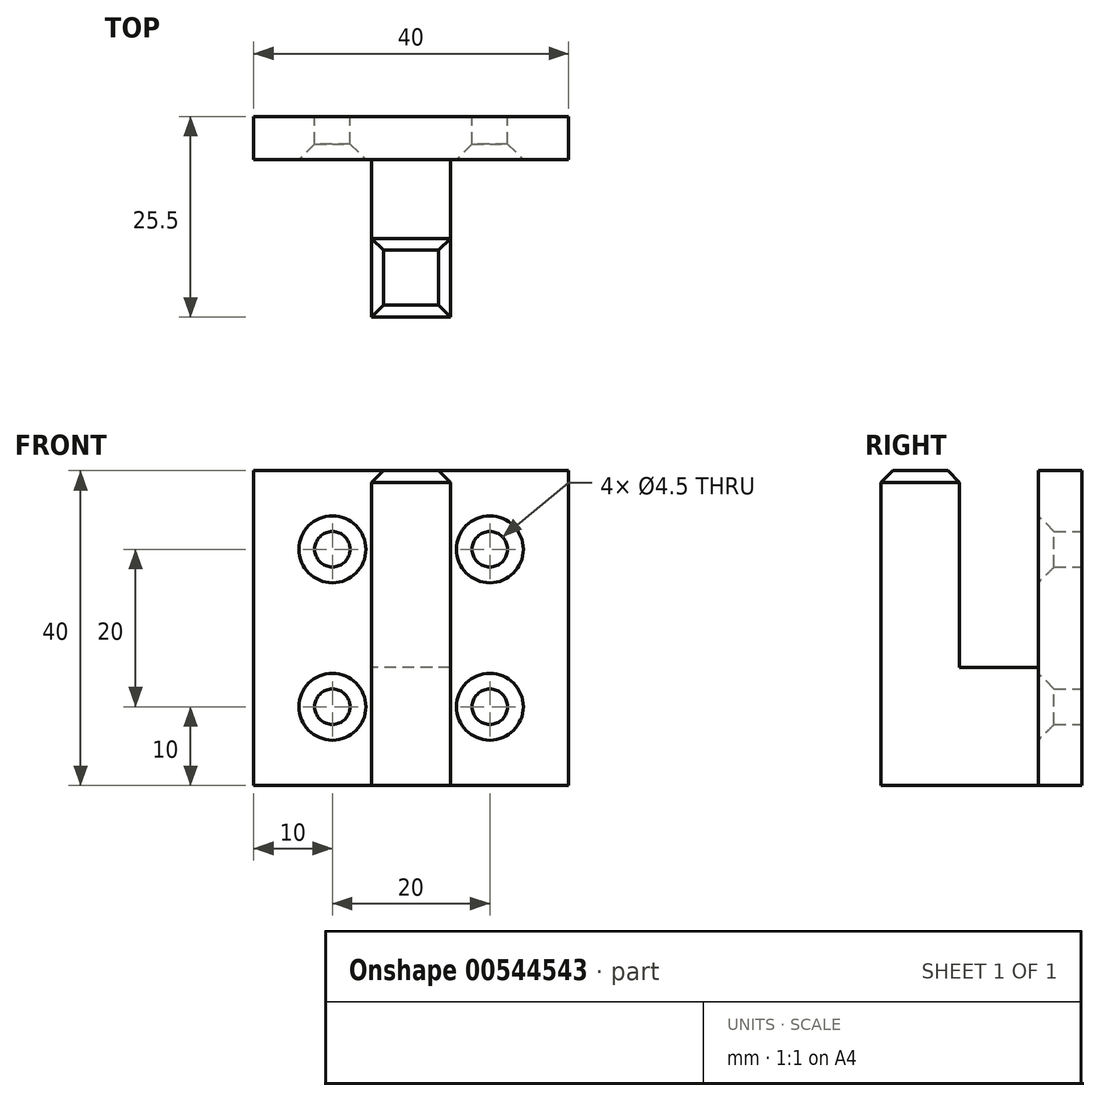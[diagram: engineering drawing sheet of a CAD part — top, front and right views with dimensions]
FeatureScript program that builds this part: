
annotation { "Feature Type Name" : "Feature", "Feature Type Description" : "" }
export const myFeature = defineFeature(function(context is Context, id is Id, definition is map)
    precondition{}
    {
        {
            var Q0;
            Q0=qCreatedBy(makeId("Front.planeOp"),FACE);
            var sketch = newSketch(context, id + "F0", { "sketchPlane" : qUnion([Q0])});
            skLineSegment(sketch, "E0", {"start": v(0, 0) * mm, "end": v(40, 0) * mm});
            skLineSegment(sketch, "E1", {"start": v(40, 0) * mm, "end": v(40, 40) * mm});
            skLineSegment(sketch, "E2", {"start": v(40, 40) * mm, "end": v(0, 40) * mm});
            skLineSegment(sketch, "E3", {"start": v(0, 40) * mm, "end": v(0, 0) * mm});
            skLineSegment(sketch, "E4", {"start": v(0, 40) * mm, "end": v(40, 0) * mm, "construction": true});
            skLineSegment(sketch, "E5", {"start": v(40, 40) * mm, "end": v(0, 0) * mm, "construction": true});
            skPoint(sketch, "E6", {"position": v(20, 20) * mm});
            skLineSegment(sketch, "E7", {"start": v(40, 40) * mm, "end": v(30, 30) * mm, "construction": true});
            skPoint(sketch, "E8", {"position": v(30, 30) * mm});
            skPoint(sketch, "E9.1.0", {"position": v(10, 30) * mm});
            skPoint(sketch, "E9.2.0", {"position": v(10, 10) * mm});
            skPoint(sketch, "E9.3.0", {"position": v(30, 10) * mm});
            skCircle(sketch, "E10", {"center": v(10, 30) * mm, "radius": 2.25 * mm});
            skCircle(sketch, "E11", {"center": v(30, 30) * mm, "radius": 2.25 * mm});
            skCircle(sketch, "E12", {"center": v(30, 10) * mm, "radius": 2.25 * mm});
            skCircle(sketch, "E13", {"center": v(10, 10) * mm, "radius": 2.25 * mm});
            skSolve(sketch);
        }
        {
            var Q0;
            Q0=makeQuery(id+"F0.imprint","IMPRINT",FACE,{"disambiguationData":[TD([[makeQuery(id+"F0.imprint","IMPRINT",EDGE,{"derivedFrom":sQuery(id+"F0.wireOp",EDGE,"E0")}),1.0]])]});
            extrude(context, id + "F1", {"entities" : qUnion([Q0]), "depth" : 5.5 * mm, "offsetDistance" : 25 * mm});
        }
        {
            var Q0;
            Q0=makeQuery(id+"F1.opExtrude","CAP_EDGE",EDGE,{"disambiguationData":[OSD([sQuery(id+"F0.wireOp",EDGE,"E10")])],"isStart":false});
            var Q1;
            Q1=makeQuery(id+"F1.opExtrude","CAP_EDGE",EDGE,{"disambiguationData":[OSD([sQuery(id+"F0.wireOp",EDGE,"E11")])],"isStart":false});
            var Q2;
            Q2=makeQuery(id+"F1.opExtrude","CAP_EDGE",EDGE,{"disambiguationData":[OSD([sQuery(id+"F0.wireOp",EDGE,"E12")])],"isStart":false});
            var Q3;
            Q3=makeQuery(id+"F1.opExtrude","CAP_EDGE",EDGE,{"disambiguationData":[OSD([sQuery(id+"F0.wireOp",EDGE,"E13")])],"isStart":false});
            chamfer(context, id + "F2", {"entities" : qUnion([Q0, Q1, Q2, Q3]), "width" : 2 * mm, "tangentPropagation" : true});
        }
        {
            var Q0;
            Q0=makeQuery(id+"F1.opExtrude","CAP_FACE",FACE,{"disambiguationData":[OSD([sQuery(id+"F0.wireOp",EDGE,"E0"),sQuery(id+"F0.wireOp",EDGE,"E1"),sQuery(id+"F0.wireOp",EDGE,"E2"),sQuery(id+"F0.wireOp",EDGE,"E3"),sQuery(id+"F0.wireOp",EDGE,"E10"),sQuery(id+"F0.wireOp",EDGE,"E11"),sQuery(id+"F0.wireOp",EDGE,"E12"),sQuery(id+"F0.wireOp",EDGE,"E13")])],"isStart":false});
            var sketch = newSketch(context, id + "F3", { "sketchPlane" : qUnion([Q0])});
            skLineSegment(sketch, "E14", {"start": v(0, 0) * mm, "end": v(15, 0) * mm, "construction": true});
            skLineSegment(sketch, "E15", {"start": v(15, 0) * mm, "end": v(25, 0) * mm});
            skLineSegment(sketch, "E16", {"start": v(25, 0) * mm, "end": v(25, 15) * mm});
            skLineSegment(sketch, "E17", {"start": v(25, 15) * mm, "end": v(15, 15) * mm});
            skLineSegment(sketch, "E18", {"start": v(15, 15) * mm, "end": v(15, 0) * mm});
            skSolve(sketch);
        }
        {
            var Q0;
            Q0 = qSketchRegion(id + "F3", true);
            extrude(context, id + "F4", {"entities" : qUnion([Q0]), "operationType" : NewBodyOperationType.ADD, "depth" : 20 * mm, "offsetDistance" : 25 * mm});
        }
        {
            var Q0;
            Q0=makeQuery(id+"F4.opExtrude","SWEPT_FACE",FACE,{"disambiguationData":[OSD([sQuery(id+"F3.wireOp",EDGE,"E17")])]});
            var sketch = newSketch(context, id + "F5", { "sketchPlane" : qUnion([Q0])});
            skLineSegment(sketch, "E19", {"start": v(15, -25.5) * mm, "end": v(25, -25.5) * mm});
            skLineSegment(sketch, "E20", {"start": v(25, -25.5) * mm, "end": v(25, -15.5) * mm});
            skLineSegment(sketch, "E21", {"start": v(25, -15.5) * mm, "end": v(15, -15.5) * mm});
            skLineSegment(sketch, "E22", {"start": v(15, -15.5) * mm, "end": v(15, -25.5) * mm});
            skSolve(sketch);
        }
        {
            var Q0;
            Q0 = qSketchRegion(id + "F5", true);
            extrude(context, id + "F6", {"entities" : qUnion([Q0]), "operationType" : NewBodyOperationType.ADD, "depth" : 25 * mm, "offsetDistance" : 25 * mm});
        }
        {
            var Q0;
            Q0=makeQuery(id+"F6.opExtrude","CAP_EDGE",EDGE,{"disambiguationData":[OSD([sQuery(id+"F5.wireOp",EDGE,"E19")])],"isStart":false});
            var Q1;
            Q1=makeQuery(id+"F6.opExtrude","CAP_EDGE",EDGE,{"disambiguationData":[OSD([sQuery(id+"F5.wireOp",EDGE,"E20")])],"isStart":false});
            var Q2;
            Q2=makeQuery(id+"F6.opExtrude","CAP_EDGE",EDGE,{"disambiguationData":[OSD([sQuery(id+"F5.wireOp",EDGE,"E21")])],"isStart":false});
            var Q3;
            Q3=makeQuery(id+"F6.opExtrude","CAP_EDGE",EDGE,{"disambiguationData":[OSD([sQuery(id+"F5.wireOp",EDGE,"E22")])],"isStart":false});
            chamfer(context, id + "F7", {"entities" : qUnion([Q0, Q1, Q2, Q3]), "width" : 1.5 * mm, "tangentPropagation" : true});
        }
    });
